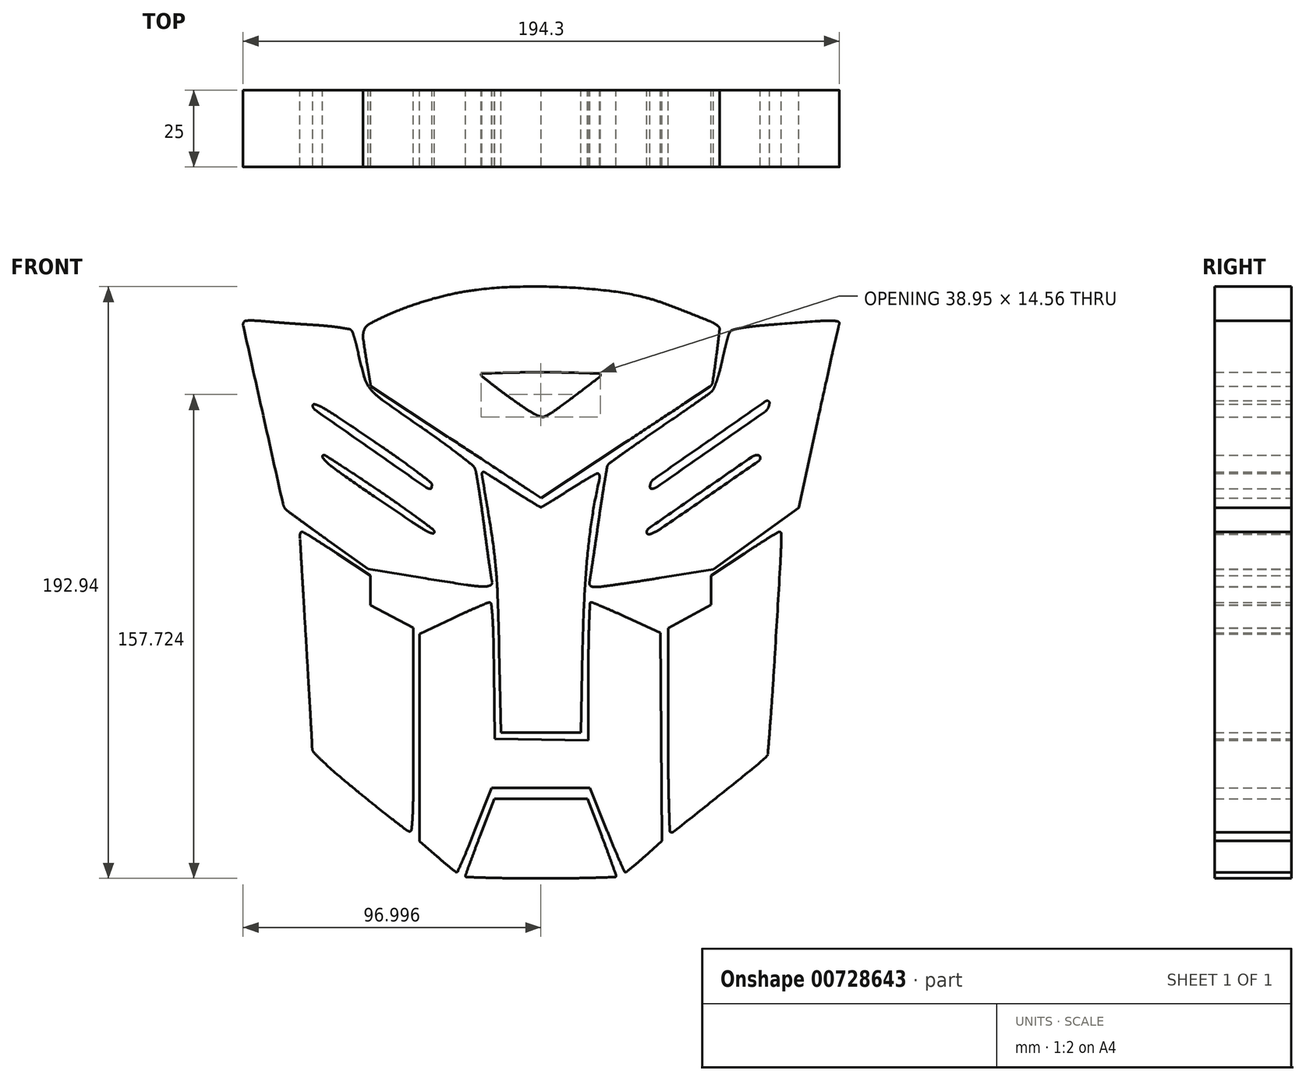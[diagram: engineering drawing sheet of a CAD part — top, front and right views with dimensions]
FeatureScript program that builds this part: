
annotation { "Feature Type Name" : "Feature", "Feature Type Description" : "" }
export const myFeature = defineFeature(function(context is Context, id is Id, definition is map)
    precondition{}
    {
        {
            var Q0;
            Q0=qCreatedBy(makeId("Front.planeOp"),FACE);
            var sketch = newSketch(context, id + "F0", { "sketchPlane" : qUnion([Q0])});
            skArc(sketch, "E0", {"start": v(-21.15, 95.4) * mm, "mid": v(-24.78, 94.86) * mm, "end": v(-28.38, 94.18) * mm});
            skArc(sketch, "E1", {"start": v(-28.38, 94.18) * mm, "mid": v(-32.1, 93.34) * mm, "end": v(-35.76, 92.36) * mm});
            skArc(sketch, "E2", {"start": v(-35.76, 92.36) * mm, "mid": v(-39.46, 91.24) * mm, "end": v(-43.12, 89.99) * mm});
            skArc(sketch, "E3", {"start": v(-43.12, 89.99) * mm, "mid": v(-46.72, 88.61) * mm, "end": v(-50.27, 87.11) * mm});
            skArc(sketch, "E4", {"start": v(-50.27, 87.11) * mm, "mid": v(-53.12, 85.79) * mm, "end": v(-55.91, 84.36) * mm});
            skArc(sketch, "E5", {"start": v(-55.91, 84.36) * mm, "mid": v(-56.96, 83.53) * mm, "end": v(-57.66, 82.4) * mm});
            skArc(sketch, "E6", {"start": v(-57.66, 82.4) * mm, "mid": v(-58.03, 80.98) * mm, "end": v(-58.02, 79.51) * mm});
            skArc(sketch, "E7", {"start": v(-58.02, 79.51) * mm, "mid": v(-57.4, 75.24) * mm, "end": v(-56.72, 70.97) * mm});
            skLineSegment(sketch, "E8", {"start": v(-56.72, 70.97) * mm, "end": v(-55.55, 64) * mm});
            skLineSegment(sketch, "E9", {"start": v(-55.55, 64) * mm, "end": v(-30.46, 47.52) * mm});
            skArc(sketch, "E10", {"start": v(-30.46, 47.52) * mm, "mid": v(-25.56, 44.3) * mm, "end": v(-20.66, 41.08) * mm});
            skArc(sketch, "E11", {"start": v(-20.66, 41.08) * mm, "mid": v(-16.31, 38.22) * mm, "end": v(-11.96, 35.37) * mm});
            skArc(sketch, "E12", {"start": v(-11.96, 35.37) * mm, "mid": v(-8.28, 32.95) * mm, "end": v(-4.6, 30.54) * mm});
            skArc(sketch, "E13", {"start": v(-4.6, 30.54) * mm, "mid": v(-3.66, 29.92) * mm, "end": v(-2.71, 29.31) * mm});
            skLineSegment(sketch, "E14", {"start": v(-2.71, 29.31) * mm, "end": v(-0.04, 27.59) * mm});
            skLineSegment(sketch, "E15", {"start": v(-0.04, 27.59) * mm, "end": v(27.4, 45.66) * mm});
            skArc(sketch, "E16", {"start": v(27.4, 45.66) * mm, "mid": v(32.68, 49.14) * mm, "end": v(37.95, 52.61) * mm});
            skArc(sketch, "E17", {"start": v(37.95, 52.61) * mm, "mid": v(42.41, 55.56) * mm, "end": v(46.87, 58.5) * mm});
            skArc(sketch, "E18", {"start": v(46.87, 58.5) * mm, "mid": v(50.88, 61.16) * mm, "end": v(54.9, 63.8) * mm});
            skArc(sketch, "E19", {"start": v(54.9, 63.8) * mm, "mid": v(55.02, 63.9) * mm, "end": v(55.14, 64) * mm});
            skArc(sketch, "E20", {"start": v(55.14, 64) * mm, "mid": v(55.63, 64.65) * mm, "end": v(55.87, 65.41) * mm});
            skArc(sketch, "E21", {"start": v(55.87, 65.41) * mm, "mid": v(56.47, 69.61) * mm, "end": v(57.04, 73.82) * mm});
            skArc(sketch, "E22", {"start": v(57.04, 73.82) * mm, "mid": v(57.6, 78.1) * mm, "end": v(58.13, 82.38) * mm});
            skArc(sketch, "E23", {"start": v(58.13, 82.38) * mm, "mid": v(58.06, 82.98) * mm, "end": v(57.72, 83.48) * mm});
            skArc(sketch, "E24", {"start": v(57.72, 83.48) * mm, "mid": v(56.62, 84.3) * mm, "end": v(55.4, 84.94) * mm});
            skArc(sketch, "E25", {"start": v(55.4, 84.94) * mm, "mid": v(51.39, 86.59) * mm, "end": v(47.37, 88.2) * mm});
            skArc(sketch, "E26", {"start": v(47.37, 88.2) * mm, "mid": v(43.36, 89.75) * mm, "end": v(39.33, 91.24) * mm});
            skArc(sketch, "E27", {"start": v(39.33, 91.24) * mm, "mid": v(36.6, 92.14) * mm, "end": v(33.85, 92.91) * mm});
            skArc(sketch, "E28", {"start": v(33.85, 92.91) * mm, "mid": v(28.04, 94.18) * mm, "end": v(22.15, 95.06) * mm});
            skArc(sketch, "E29", {"start": v(22.15, 95.06) * mm, "mid": v(14.8, 95.78) * mm, "end": v(7.43, 96.25) * mm});
            skArc(sketch, "E30", {"start": v(7.43, 96.25) * mm, "mid": v(-0.18, 96.46) * mm, "end": v(-7.79, 96.4) * mm});
            skArc(sketch, "E31", {"start": v(-7.79, 96.4) * mm, "mid": v(-14.48, 96.07) * mm, "end": v(-21.15, 95.4) * mm});
            skArc(sketch, "E32", {"start": v(19.32, 67.78) * mm, "mid": v(19.18, 67.27) * mm, "end": v(18.84, 66.86) * mm});
            skArc(sketch, "E33", {"start": v(18.84, 66.86) * mm, "mid": v(15.12, 64.02) * mm, "end": v(11.38, 61.2) * mm});
            skArc(sketch, "E34", {"start": v(11.38, 61.2) * mm, "mid": v(7.93, 58.61) * mm, "end": v(4.44, 56.06) * mm});
            skArc(sketch, "E35", {"start": v(4.44, 56.06) * mm, "mid": v(2.9, 55.04) * mm, "end": v(1.28, 54.16) * mm});
            skArc(sketch, "E36", {"start": v(1.28, 54.16) * mm, "mid": v(0.62, 53.98) * mm, "end": v(-0.06, 54.05) * mm});
            skArc(sketch, "E37", {"start": v(-0.06, 54.05) * mm, "mid": v(-1.12, 54.43) * mm, "end": v(-2.14, 54.91) * mm});
            skArc(sketch, "E38", {"start": v(-2.14, 54.91) * mm, "mid": v(-3.69, 55.79) * mm, "end": v(-5.18, 56.75) * mm});
            skArc(sketch, "E39", {"start": v(-5.18, 56.75) * mm, "mid": v(-7.63, 58.44) * mm, "end": v(-10.06, 60.16) * mm});
            skArc(sketch, "E40", {"start": v(-10.06, 60.16) * mm, "mid": v(-11.9, 61.5) * mm, "end": v(-13.72, 62.85) * mm});
            skArc(sketch, "E41", {"start": v(-13.72, 62.85) * mm, "mid": v(-15.27, 64.03) * mm, "end": v(-16.8, 65.23) * mm});
            skArc(sketch, "E42", {"start": v(-16.8, 65.23) * mm, "mid": v(-18.1, 66.28) * mm, "end": v(-19.4, 67.32) * mm});
            skArc(sketch, "E43", {"start": v(-19.4, 67.32) * mm, "mid": v(-19.56, 67.53) * mm, "end": v(-19.63, 67.78) * mm});
            skArc(sketch, "E44", {"start": v(-19.63, 67.78) * mm, "mid": v(-19.55, 68) * mm, "end": v(-19.34, 68.09) * mm});
            skArc(sketch, "E45", {"start": v(-19.34, 68.09) * mm, "mid": v(-16.63, 68.2) * mm, "end": v(-13.91, 68.31) * mm});
            skArc(sketch, "E46", {"start": v(-13.91, 68.31) * mm, "mid": v(-10.77, 68.41) * mm, "end": v(-7.62, 68.48) * mm});
            skArc(sketch, "E47", {"start": v(-7.62, 68.48) * mm, "mid": v(-3.89, 68.52) * mm, "end": v(-0.15, 68.53) * mm});
            skArc(sketch, "E48", {"start": v(-0.15, 68.53) * mm, "mid": v(3.59, 68.52) * mm, "end": v(7.33, 68.48) * mm});
            skArc(sketch, "E49", {"start": v(7.33, 68.48) * mm, "mid": v(10.47, 68.41) * mm, "end": v(13.61, 68.31) * mm});
            skArc(sketch, "E50", {"start": v(13.61, 68.31) * mm, "mid": v(16.33, 68.2) * mm, "end": v(19.04, 68.09) * mm});
            skArc(sketch, "E51", {"start": v(19.04, 68.09) * mm, "mid": v(19.24, 68) * mm, "end": v(19.32, 67.78) * mm});
            skArc(sketch, "E52", {"start": v(-96.73, 85.14) * mm, "mid": v(-97.1, 84.5) * mm, "end": v(-97.11, 83.79) * mm});
            skArc(sketch, "E53", {"start": v(-97.11, 83.79) * mm, "mid": v(-93.86, 69.13) * mm, "end": v(-90.6, 54.47) * mm});
            skArc(sketch, "E54", {"start": v(-90.6, 54.47) * mm, "mid": v(-87.37, 39.96) * mm, "end": v(-84.12, 25.45) * mm});
            skArc(sketch, "E55", {"start": v(-84.12, 25.45) * mm, "mid": v(-83.72, 24.45) * mm, "end": v(-83.03, 23.63) * mm});
            skArc(sketch, "E56", {"start": v(-83.03, 23.63) * mm, "mid": v(-82.7, 23.34) * mm, "end": v(-82.35, 23.08) * mm});
            skArc(sketch, "E57", {"start": v(-82.35, 23.08) * mm, "mid": v(-80.5, 21.72) * mm, "end": v(-78.64, 20.36) * mm});
            skArc(sketch, "E58", {"start": v(-78.64, 20.36) * mm, "mid": v(-76.47, 18.78) * mm, "end": v(-74.3, 17.2) * mm});
            skArc(sketch, "E59", {"start": v(-74.3, 17.2) * mm, "mid": v(-71.8, 15.4) * mm, "end": v(-69.31, 13.6) * mm});
            skLineSegment(sketch, "E60", {"start": v(-69.31, 13.6) * mm, "end": v(-56.47, 4.38) * mm});
            skLineSegment(sketch, "E61", {"start": v(-56.47, 4.38) * mm, "end": v(-38.5, 1.45) * mm});
            skArc(sketch, "E62", {"start": v(-38.5, 1.45) * mm, "mid": v(-31.44, 0.32) * mm, "end": v(-24.38, -0.78) * mm});
            skArc(sketch, "E63", {"start": v(-24.38, -0.78) * mm, "mid": v(-21.68, -1.13) * mm, "end": v(-18.96, -1.34) * mm});
            skArc(sketch, "E64", {"start": v(-18.96, -1.34) * mm, "mid": v(-17.77, -1.27) * mm, "end": v(-16.63, -0.96) * mm});
            skArc(sketch, "E65", {"start": v(-16.63, -0.96) * mm, "mid": v(-16.08, -0.45) * mm, "end": v(-16.01, 0.28) * mm});
            skArc(sketch, "E66", {"start": v(-16.01, 0.28) * mm, "mid": v(-16.17, 0.9) * mm, "end": v(-16.28, 1.54) * mm});
            skArc(sketch, "E67", {"start": v(-16.28, 1.54) * mm, "mid": v(-16.64, 3.95) * mm, "end": v(-17, 6.37) * mm});
            skArc(sketch, "E68", {"start": v(-17, 6.37) * mm, "mid": v(-17.4, 9.22) * mm, "end": v(-17.79, 12.08) * mm});
            skArc(sketch, "E69", {"start": v(-17.79, 12.08) * mm, "mid": v(-18.22, 15.3) * mm, "end": v(-18.64, 18.53) * mm});
            skArc(sketch, "E70", {"start": v(-18.64, 18.53) * mm, "mid": v(-19.07, 21.77) * mm, "end": v(-19.51, 25) * mm});
            skArc(sketch, "E71", {"start": v(-19.51, 25) * mm, "mid": v(-19.94, 27.9) * mm, "end": v(-20.39, 30.8) * mm});
            skArc(sketch, "E72", {"start": v(-20.39, 30.8) * mm, "mid": v(-20.78, 33.22) * mm, "end": v(-21.19, 35.64) * mm});
            skArc(sketch, "E73", {"start": v(-21.19, 35.64) * mm, "mid": v(-21.35, 36.38) * mm, "end": v(-21.6, 37.1) * mm});
            skArc(sketch, "E74", {"start": v(-21.6, 37.1) * mm, "mid": v(-21.97, 37.76) * mm, "end": v(-22.5, 38.3) * mm});
            skArc(sketch, "E75", {"start": v(-22.5, 38.3) * mm, "mid": v(-24.84, 40.16) * mm, "end": v(-27.2, 42) * mm});
            skArc(sketch, "E76", {"start": v(-27.2, 42) * mm, "mid": v(-30.03, 44.13) * mm, "end": v(-32.9, 46.23) * mm});
            skArc(sketch, "E77", {"start": v(-32.9, 46.23) * mm, "mid": v(-36.19, 48.57) * mm, "end": v(-39.5, 50.87) * mm});
            skArc(sketch, "E78", {"start": v(-39.5, 50.87) * mm, "mid": v(-45.65, 55.14) * mm, "end": v(-51.77, 59.45) * mm});
            skArc(sketch, "E79", {"start": v(-51.77, 59.45) * mm, "mid": v(-53.78, 61.1) * mm, "end": v(-55.57, 63) * mm});
            skArc(sketch, "E80", {"start": v(-55.57, 63) * mm, "mid": v(-56.82, 64.87) * mm, "end": v(-57.66, 66.96) * mm});
            skArc(sketch, "E81", {"start": v(-57.66, 66.96) * mm, "mid": v(-58.79, 71.2) * mm, "end": v(-59.78, 75.45) * mm});
            skArc(sketch, "E82", {"start": v(-59.78, 75.45) * mm, "mid": v(-60.03, 76.56) * mm, "end": v(-60.3, 77.67) * mm});
            skArc(sketch, "E83", {"start": v(-60.3, 77.67) * mm, "mid": v(-60.57, 78.7) * mm, "end": v(-60.87, 79.72) * mm});
            skArc(sketch, "E84", {"start": v(-60.87, 79.72) * mm, "mid": v(-61.14, 80.57) * mm, "end": v(-61.42, 81.4) * mm});
            skArc(sketch, "E85", {"start": v(-61.42, 81.4) * mm, "mid": v(-61.59, 81.79) * mm, "end": v(-61.81, 82.14) * mm});
            skArc(sketch, "E86", {"start": v(-61.81, 82.14) * mm, "mid": v(-62.14, 82.44) * mm, "end": v(-62.56, 82.6) * mm});
            skArc(sketch, "E87", {"start": v(-62.56, 82.6) * mm, "mid": v(-64.06, 82.87) * mm, "end": v(-65.56, 83.11) * mm});
            skArc(sketch, "E88", {"start": v(-65.56, 83.11) * mm, "mid": v(-67.39, 83.37) * mm, "end": v(-69.22, 83.57) * mm});
            skArc(sketch, "E89", {"start": v(-69.22, 83.57) * mm, "mid": v(-71.3, 83.76) * mm, "end": v(-73.4, 83.9) * mm});
            skArc(sketch, "E90", {"start": v(-73.4, 83.9) * mm, "mid": v(-75.68, 84.05) * mm, "end": v(-77.95, 84.2) * mm});
            skArc(sketch, "E91", {"start": v(-77.95, 84.2) * mm, "mid": v(-80.35, 84.38) * mm, "end": v(-82.75, 84.55) * mm});
            skArc(sketch, "E92", {"start": v(-82.75, 84.55) * mm, "mid": v(-84.93, 84.72) * mm, "end": v(-87.11, 84.9) * mm});
            skArc(sketch, "E93", {"start": v(-87.11, 84.9) * mm, "mid": v(-88.63, 85.02) * mm, "end": v(-90.15, 85.16) * mm});
            skArc(sketch, "E94", {"start": v(-90.15, 85.16) * mm, "mid": v(-91.32, 85.26) * mm, "end": v(-92.49, 85.34) * mm});
            skArc(sketch, "E95", {"start": v(-92.49, 85.34) * mm, "mid": v(-93.52, 85.38) * mm, "end": v(-94.56, 85.4) * mm});
            skArc(sketch, "E96", {"start": v(-94.56, 85.4) * mm, "mid": v(-95.4, 85.38) * mm, "end": v(-96.25, 85.35) * mm});
            skArc(sketch, "E97", {"start": v(-96.25, 85.35) * mm, "mid": v(-96.51, 85.29) * mm, "end": v(-96.73, 85.14) * mm});
            skArc(sketch, "E98", {"start": v(-53.56, 45.36) * mm, "mid": v(-50.12, 43) * mm, "end": v(-46.7, 40.6) * mm});
            skArc(sketch, "E99", {"start": v(-46.7, 40.6) * mm, "mid": v(-43.79, 38.51) * mm, "end": v(-40.9, 36.38) * mm});
            skArc(sketch, "E100", {"start": v(-40.9, 36.38) * mm, "mid": v(-38.47, 34.53) * mm, "end": v(-36.04, 32.67) * mm});
            skArc(sketch, "E101", {"start": v(-36.04, 32.67) * mm, "mid": v(-35.75, 32.32) * mm, "end": v(-35.65, 31.87) * mm});
            skArc(sketch, "E102", {"start": v(-35.65, 31.87) * mm, "mid": v(-35.65, 31.61) * mm, "end": v(-35.67, 31.36) * mm});
            skArc(sketch, "E103", {"start": v(-35.67, 31.36) * mm, "mid": v(-35.7, 31.14) * mm, "end": v(-35.75, 30.92) * mm});
            skArc(sketch, "E104", {"start": v(-35.75, 30.92) * mm, "mid": v(-35.8, 30.77) * mm, "end": v(-35.86, 30.62) * mm});
            skArc(sketch, "E105", {"start": v(-35.86, 30.62) * mm, "mid": v(-35.92, 30.56) * mm, "end": v(-36, 30.53) * mm});
            skArc(sketch, "E106", {"start": v(-36, 30.53) * mm, "mid": v(-36.86, 30.67) * mm, "end": v(-37.65, 31.05) * mm});
            skArc(sketch, "E107", {"start": v(-37.65, 31.05) * mm, "mid": v(-46.62, 37.3) * mm, "end": v(-55.58, 43.56) * mm});
            skArc(sketch, "E108", {"start": v(-55.58, 43.56) * mm, "mid": v(-64.56, 49.85) * mm, "end": v(-73.53, 56.14) * mm});
            skArc(sketch, "E109", {"start": v(-73.53, 56.14) * mm, "mid": v(-74.11, 56.71) * mm, "end": v(-74.48, 57.44) * mm});
            skArc(sketch, "E110", {"start": v(-74.48, 57.44) * mm, "mid": v(-74.36, 57.96) * mm, "end": v(-73.84, 58.1) * mm});
            skArc(sketch, "E111", {"start": v(-73.84, 58.1) * mm, "mid": v(-72.58, 57.69) * mm, "end": v(-71.39, 57.1) * mm});
            skArc(sketch, "E112", {"start": v(-71.39, 57.1) * mm, "mid": v(-68.65, 55.46) * mm, "end": v(-65.97, 53.73) * mm});
            skArc(sketch, "E113", {"start": v(-65.97, 53.73) * mm, "mid": v(-59.76, 49.56) * mm, "end": v(-53.56, 45.36) * mm});
            skArc(sketch, "E114", {"start": v(-52.65, 29.76) * mm, "mid": v(-49.3, 27.47) * mm, "end": v(-45.96, 25.15) * mm});
            skArc(sketch, "E115", {"start": v(-45.96, 25.15) * mm, "mid": v(-43.1, 23.11) * mm, "end": v(-40.26, 21.04) * mm});
            skArc(sketch, "E116", {"start": v(-40.26, 21.04) * mm, "mid": v(-37.85, 19.25) * mm, "end": v(-35.44, 17.44) * mm});
            skArc(sketch, "E117", {"start": v(-35.44, 17.44) * mm, "mid": v(-35.08, 17.07) * mm, "end": v(-34.84, 16.6) * mm});
            skArc(sketch, "E118", {"start": v(-34.84, 16.6) * mm, "mid": v(-34.93, 16.14) * mm, "end": v(-35.38, 16) * mm});
            skArc(sketch, "E119", {"start": v(-35.38, 16) * mm, "mid": v(-36.43, 16.31) * mm, "end": v(-37.42, 16.8) * mm});
            skArc(sketch, "E120", {"start": v(-37.42, 16.8) * mm, "mid": v(-39.85, 18.27) * mm, "end": v(-42.23, 19.81) * mm});
            skArc(sketch, "E121", {"start": v(-42.23, 19.81) * mm, "mid": v(-48.32, 23.92) * mm, "end": v(-54.4, 28.05) * mm});
            skArc(sketch, "E122", {"start": v(-54.4, 28.05) * mm, "mid": v(-59.42, 31.49) * mm, "end": v(-64.42, 34.96) * mm});
            skArc(sketch, "E123", {"start": v(-64.42, 34.96) * mm, "mid": v(-66.94, 36.8) * mm, "end": v(-69.4, 38.74) * mm});
            skArc(sketch, "E124", {"start": v(-69.4, 38.74) * mm, "mid": v(-70.39, 39.67) * mm, "end": v(-71.24, 40.72) * mm});
            skArc(sketch, "E125", {"start": v(-71.24, 40.72) * mm, "mid": v(-71.28, 41.26) * mm, "end": v(-70.82, 41.53) * mm});
            skArc(sketch, "E126", {"start": v(-70.82, 41.53) * mm, "mid": v(-70.51, 41.49) * mm, "end": v(-70.23, 41.36) * mm});
            skArc(sketch, "E127", {"start": v(-70.23, 41.36) * mm, "mid": v(-67.68, 39.72) * mm, "end": v(-65.14, 38.07) * mm});
            skArc(sketch, "E128", {"start": v(-65.14, 38.07) * mm, "mid": v(-62.24, 36.18) * mm, "end": v(-59.36, 34.27) * mm});
            skArc(sketch, "E129", {"start": v(-59.36, 34.27) * mm, "mid": v(-56, 32.02) * mm, "end": v(-52.65, 29.76) * mm});
            skArc(sketch, "E130", {"start": v(76.03, 84.13) * mm, "mid": v(72.61, 83.85) * mm, "end": v(69.2, 83.52) * mm});
            skArc(sketch, "E131", {"start": v(69.2, 83.52) * mm, "mid": v(67.1, 83.28) * mm, "end": v(65.02, 82.95) * mm});
            skArc(sketch, "E132", {"start": v(65.02, 82.95) * mm, "mid": v(63.7, 82.67) * mm, "end": v(62.37, 82.33) * mm});
            skArc(sketch, "E133", {"start": v(62.37, 82.33) * mm, "mid": v(61.8, 82.03) * mm, "end": v(61.4, 81.53) * mm});
            skArc(sketch, "E134", {"start": v(61.4, 81.53) * mm, "mid": v(61.16, 81.05) * mm, "end": v(60.99, 80.54) * mm});
            skArc(sketch, "E135", {"start": v(60.99, 80.54) * mm, "mid": v(60.64, 79.3) * mm, "end": v(60.3, 78.06) * mm});
            skArc(sketch, "E136", {"start": v(60.3, 78.06) * mm, "mid": v(59.92, 76.57) * mm, "end": v(59.56, 75.07) * mm});
            skArc(sketch, "E137", {"start": v(59.56, 75.07) * mm, "mid": v(59.19, 73.44) * mm, "end": v(58.83, 71.81) * mm});
            skArc(sketch, "E138", {"start": v(58.83, 71.81) * mm, "mid": v(58.46, 70.18) * mm, "end": v(58.04, 68.56) * mm});
            skArc(sketch, "E139", {"start": v(58.04, 68.56) * mm, "mid": v(57.6, 67.07) * mm, "end": v(57.12, 65.6) * mm});
            skArc(sketch, "E140", {"start": v(57.12, 65.6) * mm, "mid": v(56.67, 64.39) * mm, "end": v(56.19, 63.2) * mm});
            skArc(sketch, "E141", {"start": v(56.19, 63.2) * mm, "mid": v(55.88, 62.65) * mm, "end": v(55.46, 62.2) * mm});
            skArc(sketch, "E142", {"start": v(55.46, 62.2) * mm, "mid": v(54.89, 61.72) * mm, "end": v(54.28, 61.27) * mm});
            skArc(sketch, "E143", {"start": v(54.28, 61.27) * mm, "mid": v(51.99, 59.66) * mm, "end": v(49.7, 58.04) * mm});
            skArc(sketch, "E144", {"start": v(49.7, 58.04) * mm, "mid": v(46.97, 56.14) * mm, "end": v(44.24, 54.25) * mm});
            skArc(sketch, "E145", {"start": v(44.24, 54.25) * mm, "mid": v(41.16, 52.13) * mm, "end": v(38.07, 50.02) * mm});
            skArc(sketch, "E146", {"start": v(38.07, 50.02) * mm, "mid": v(35.02, 47.93) * mm, "end": v(31.98, 45.83) * mm});
            skArc(sketch, "E147", {"start": v(31.98, 45.83) * mm, "mid": v(29.37, 44) * mm, "end": v(26.76, 42.14) * mm});
            skArc(sketch, "E148", {"start": v(26.76, 42.14) * mm, "mid": v(24.52, 40.53) * mm, "end": v(22.27, 38.92) * mm});
            skArc(sketch, "E149", {"start": v(22.27, 38.92) * mm, "mid": v(21.97, 38.65) * mm, "end": v(21.73, 38.33) * mm});
            skArc(sketch, "E150", {"start": v(21.73, 38.33) * mm, "mid": v(21.55, 37.97) * mm, "end": v(21.44, 37.59) * mm});
            skArc(sketch, "E151", {"start": v(21.44, 37.59) * mm, "mid": v(21.03, 35.18) * mm, "end": v(20.63, 32.78) * mm});
            skArc(sketch, "E152", {"start": v(20.63, 32.78) * mm, "mid": v(20.17, 29.98) * mm, "end": v(19.73, 27.19) * mm});
            skArc(sketch, "E153", {"start": v(19.73, 27.19) * mm, "mid": v(19.25, 23.96) * mm, "end": v(18.78, 20.72) * mm});
            skArc(sketch, "E154", {"start": v(18.78, 20.72) * mm, "mid": v(18.31, 17.43) * mm, "end": v(17.83, 14.13) * mm});
            skArc(sketch, "E155", {"start": v(17.83, 14.13) * mm, "mid": v(17.4, 11.13) * mm, "end": v(16.96, 8.13) * mm});
            skArc(sketch, "E156", {"start": v(16.96, 8.13) * mm, "mid": v(16.58, 5.61) * mm, "end": v(16.2, 3.1) * mm});
            skArc(sketch, "E157", {"start": v(16.2, 3.1) * mm, "mid": v(16.06, 2.19) * mm, "end": v(15.9, 1.28) * mm});
            skArc(sketch, "E158", {"start": v(15.9, 1.28) * mm, "mid": v(15.78, 0.5) * mm, "end": v(15.7, -0.28) * mm});
            skArc(sketch, "E159", {"start": v(15.7, -0.28) * mm, "mid": v(15.75, -0.67) * mm, "end": v(15.94, -1) * mm});
            skArc(sketch, "E160", {"start": v(15.94, -1) * mm, "mid": v(16.23, -1.25) * mm, "end": v(16.6, -1.37) * mm});
            skArc(sketch, "E161", {"start": v(16.6, -1.37) * mm, "mid": v(17.36, -1.43) * mm, "end": v(18.13, -1.44) * mm});
            skArc(sketch, "E162", {"start": v(18.13, -1.44) * mm, "mid": v(19.04, -1.4) * mm, "end": v(19.94, -1.32) * mm});
            skArc(sketch, "E163", {"start": v(19.94, -1.32) * mm, "mid": v(22.58, -0.96) * mm, "end": v(25.22, -0.59) * mm});
            skArc(sketch, "E164", {"start": v(25.22, -0.59) * mm, "mid": v(28.37, -0.13) * mm, "end": v(31.5, 0.34) * mm});
            skArc(sketch, "E165", {"start": v(31.5, 0.34) * mm, "mid": v(34.98, 0.89) * mm, "end": v(38.45, 1.44) * mm});
            skLineSegment(sketch, "E166", {"start": v(38.45, 1.44) * mm, "end": v(56.04, 4.31) * mm});
            skLineSegment(sketch, "E167", {"start": v(56.04, 4.31) * mm, "end": v(69.95, 14.35) * mm});
            skLineSegment(sketch, "E168", {"start": v(69.95, 14.35) * mm, "end": v(83.85, 24.4) * mm});
            skLineSegment(sketch, "E169", {"start": v(83.85, 24.4) * mm, "end": v(90.25, 53.71) * mm});
            skArc(sketch, "E170", {"start": v(90.25, 53.71) * mm, "mid": v(91.5, 59.38) * mm, "end": v(92.74, 65.04) * mm});
            skArc(sketch, "E171", {"start": v(92.74, 65.04) * mm, "mid": v(93.82, 69.92) * mm, "end": v(94.9, 74.79) * mm});
            skArc(sketch, "E172", {"start": v(94.9, 74.79) * mm, "mid": v(95.86, 79.04) * mm, "end": v(96.82, 83.3) * mm});
            skArc(sketch, "E173", {"start": v(96.82, 83.3) * mm, "mid": v(96.95, 83.8) * mm, "end": v(97.1, 84.28) * mm});
            skArc(sketch, "E174", {"start": v(97.1, 84.28) * mm, "mid": v(97.07, 84.8) * mm, "end": v(96.65, 85.11) * mm});
            skArc(sketch, "E175", {"start": v(96.65, 85.11) * mm, "mid": v(95.47, 85.3) * mm, "end": v(94.28, 85.35) * mm});
            skArc(sketch, "E176", {"start": v(94.28, 85.35) * mm, "mid": v(91.75, 85.3) * mm, "end": v(89.22, 85.15) * mm});
            skArc(sketch, "E177", {"start": v(89.22, 85.15) * mm, "mid": v(82.62, 84.65) * mm, "end": v(76.03, 84.13) * mm});
            skArc(sketch, "E178", {"start": v(74.05, 57.2) * mm, "mid": v(73.57, 56.35) * mm, "end": v(72.87, 55.68) * mm});
            skArc(sketch, "E179", {"start": v(72.87, 55.68) * mm, "mid": v(64.07, 49.52) * mm, "end": v(55.26, 43.37) * mm});
            skArc(sketch, "E180", {"start": v(55.26, 43.37) * mm, "mid": v(46.44, 37.23) * mm, "end": v(37.61, 31.1) * mm});
            skArc(sketch, "E181", {"start": v(37.61, 31.1) * mm, "mid": v(36.76, 30.68) * mm, "end": v(35.82, 30.53) * mm});
            skArc(sketch, "E182", {"start": v(35.82, 30.53) * mm, "mid": v(35.7, 30.56) * mm, "end": v(35.6, 30.65) * mm});
            skArc(sketch, "E183", {"start": v(35.6, 30.65) * mm, "mid": v(35.53, 30.8) * mm, "end": v(35.48, 30.97) * mm});
            skArc(sketch, "E184", {"start": v(35.48, 30.97) * mm, "mid": v(35.45, 31.2) * mm, "end": v(35.45, 31.45) * mm});
            skArc(sketch, "E185", {"start": v(35.45, 31.45) * mm, "mid": v(35.48, 31.74) * mm, "end": v(35.53, 32.02) * mm});
            skArc(sketch, "E186", {"start": v(35.53, 32.02) * mm, "mid": v(35.92, 32.94) * mm, "end": v(36.62, 33.66) * mm});
            skArc(sketch, "E187", {"start": v(36.62, 33.66) * mm, "mid": v(45.66, 40) * mm, "end": v(54.72, 46.31) * mm});
            skArc(sketch, "E188", {"start": v(54.72, 46.31) * mm, "mid": v(63.9, 52.7) * mm, "end": v(73.08, 59.07) * mm});
            skArc(sketch, "E189", {"start": v(73.08, 59.07) * mm, "mid": v(73.67, 59.23) * mm, "end": v(74.23, 58.98) * mm});
            skArc(sketch, "E190", {"start": v(74.23, 58.98) * mm, "mid": v(74.3, 58.87) * mm, "end": v(74.33, 58.75) * mm});
            skArc(sketch, "E191", {"start": v(74.33, 58.75) * mm, "mid": v(74.34, 58.53) * mm, "end": v(74.33, 58.3) * mm});
            skArc(sketch, "E192", {"start": v(74.33, 58.3) * mm, "mid": v(74.3, 58.03) * mm, "end": v(74.23, 57.77) * mm});
            skArc(sketch, "E193", {"start": v(74.23, 57.77) * mm, "mid": v(74.15, 57.48) * mm, "end": v(74.05, 57.2) * mm});
            skArc(sketch, "E194", {"start": v(71.35, 40.59) * mm, "mid": v(71.22, 40.03) * mm, "end": v(70.84, 39.6) * mm});
            skArc(sketch, "E195", {"start": v(70.84, 39.6) * mm, "mid": v(62.7, 33.94) * mm, "end": v(54.55, 28.3) * mm});
            skArc(sketch, "E196", {"start": v(54.55, 28.3) * mm, "mid": v(46.88, 22.99) * mm, "end": v(39.18, 17.7) * mm});
            skArc(sketch, "E197", {"start": v(39.18, 17.7) * mm, "mid": v(37.45, 16.65) * mm, "end": v(35.6, 15.8) * mm});
            skArc(sketch, "E198", {"start": v(35.6, 15.8) * mm, "mid": v(35.37, 15.74) * mm, "end": v(35.12, 15.7) * mm});
            skArc(sketch, "E199", {"start": v(35.12, 15.7) * mm, "mid": v(34.92, 15.71) * mm, "end": v(34.72, 15.77) * mm});
            skArc(sketch, "E200", {"start": v(34.72, 15.77) * mm, "mid": v(34.57, 15.87) * mm, "end": v(34.45, 16.02) * mm});
            skArc(sketch, "E201", {"start": v(34.45, 16.02) * mm, "mid": v(34.38, 16.2) * mm, "end": v(34.35, 16.38) * mm});
            skArc(sketch, "E202", {"start": v(34.35, 16.38) * mm, "mid": v(34.52, 17.06) * mm, "end": v(34.98, 17.59) * mm});
            skArc(sketch, "E203", {"start": v(34.98, 17.59) * mm, "mid": v(43.42, 23.48) * mm, "end": v(51.87, 29.36) * mm});
            skArc(sketch, "E204", {"start": v(51.87, 29.36) * mm, "mid": v(60.2, 35.14) * mm, "end": v(68.55, 40.92) * mm});
            skArc(sketch, "E205", {"start": v(68.55, 40.92) * mm, "mid": v(69.5, 41.38) * mm, "end": v(70.53, 41.53) * mm});
            skArc(sketch, "E206", {"start": v(70.53, 41.53) * mm, "mid": v(70.7, 41.51) * mm, "end": v(70.84, 41.46) * mm});
            skArc(sketch, "E207", {"start": v(70.84, 41.46) * mm, "mid": v(70.99, 41.37) * mm, "end": v(71.11, 41.25) * mm});
            skArc(sketch, "E208", {"start": v(71.11, 41.25) * mm, "mid": v(71.22, 41.1) * mm, "end": v(71.3, 40.95) * mm});
            skArc(sketch, "E209", {"start": v(71.3, 40.95) * mm, "mid": v(71.34, 40.77) * mm, "end": v(71.35, 40.59) * mm});
            skArc(sketch, "E210", {"start": v(-19.13, 33.83) * mm, "mid": v(-17.67, 25.16) * mm, "end": v(-16.26, 16.48) * mm});
            skArc(sketch, "E211", {"start": v(-16.26, 16.48) * mm, "mid": v(-15.5, 11.18) * mm, "end": v(-14.91, 5.86) * mm});
            skArc(sketch, "E212", {"start": v(-14.91, 5.86) * mm, "mid": v(-14.48, 0.56) * mm, "end": v(-14.2, -4.75) * mm});
            skArc(sketch, "E213", {"start": v(-14.2, -4.75) * mm, "mid": v(-13.92, -13.36) * mm, "end": v(-13.71, -21.97) * mm});
            skLineSegment(sketch, "E214", {"start": v(-13.71, -21.97) * mm, "end": v(-13.15, -48.97) * mm});
            skLineSegment(sketch, "E215", {"start": v(-13.15, -48.97) * mm, "end": v(-0.15, -48.97) * mm});
            skLineSegment(sketch, "E216", {"start": v(-0.15, -48.97) * mm, "end": v(12.85, -48.97) * mm});
            skLineSegment(sketch, "E217", {"start": v(12.85, -48.97) * mm, "end": v(13.45, -21.97) * mm});
            skArc(sketch, "E218", {"start": v(13.45, -21.97) * mm, "mid": v(13.7, -13.31) * mm, "end": v(14.07, -4.66) * mm});
            skArc(sketch, "E219", {"start": v(14.07, -4.66) * mm, "mid": v(14.5, 2.47) * mm, "end": v(15.12, 9.59) * mm});
            skArc(sketch, "E220", {"start": v(15.12, 9.59) * mm, "mid": v(15.82, 15.76) * mm, "end": v(16.69, 21.92) * mm});
            skArc(sketch, "E221", {"start": v(16.69, 21.92) * mm, "mid": v(17.68, 27.62) * mm, "end": v(18.87, 33.28) * mm});
            skArc(sketch, "E222", {"start": v(18.87, 33.28) * mm, "mid": v(18.95, 33.71) * mm, "end": v(19, 34.15) * mm});
            skArc(sketch, "E223", {"start": v(19, 34.15) * mm, "mid": v(19, 34.51) * mm, "end": v(18.95, 34.87) * mm});
            skArc(sketch, "E224", {"start": v(18.95, 34.87) * mm, "mid": v(18.87, 35.13) * mm, "end": v(18.74, 35.36) * mm});
            skArc(sketch, "E225", {"start": v(18.74, 35.36) * mm, "mid": v(18.6, 35.49) * mm, "end": v(18.4, 35.53) * mm});
            skArc(sketch, "E226", {"start": v(18.4, 35.53) * mm, "mid": v(18.07, 35.49) * mm, "end": v(17.75, 35.36) * mm});
            skArc(sketch, "E227", {"start": v(17.75, 35.36) * mm, "mid": v(16.47, 34.64) * mm, "end": v(15.2, 33.92) * mm});
            skArc(sketch, "E228", {"start": v(15.2, 33.92) * mm, "mid": v(13.71, 33.04) * mm, "end": v(12.23, 32.14) * mm});
            skArc(sketch, "E229", {"start": v(12.23, 32.14) * mm, "mid": v(10.56, 31.1) * mm, "end": v(8.9, 30.03) * mm});
            skArc(sketch, "E230", {"start": v(8.9, 30.03) * mm, "mid": v(7.25, 28.98) * mm, "end": v(5.6, 27.92) * mm});
            skArc(sketch, "E231", {"start": v(5.6, 27.92) * mm, "mid": v(4.17, 27.03) * mm, "end": v(2.74, 26.15) * mm});
            skArc(sketch, "E232", {"start": v(2.74, 26.15) * mm, "mid": v(1.49, 25.39) * mm, "end": v(0.24, 24.63) * mm});
            skArc(sketch, "E233", {"start": v(0.24, 24.63) * mm, "mid": v(0.07, 24.56) * mm, "end": v(-0.1, 24.53) * mm});
            skArc(sketch, "E234", {"start": v(-0.1, 24.53) * mm, "mid": v(-0.28, 24.56) * mm, "end": v(-0.44, 24.63) * mm});
            skArc(sketch, "E235", {"start": v(-0.44, 24.63) * mm, "mid": v(-1.66, 25.36) * mm, "end": v(-2.87, 26.1) * mm});
            skArc(sketch, "E236", {"start": v(-2.87, 26.1) * mm, "mid": v(-4.27, 26.95) * mm, "end": v(-5.65, 27.81) * mm});
            skArc(sketch, "E237", {"start": v(-5.65, 27.81) * mm, "mid": v(-7.26, 28.83) * mm, "end": v(-8.86, 29.85) * mm});
            skArc(sketch, "E238", {"start": v(-8.86, 29.85) * mm, "mid": v(-10.5, 30.9) * mm, "end": v(-12.13, 31.94) * mm});
            skArc(sketch, "E239", {"start": v(-12.13, 31.94) * mm, "mid": v(-13.6, 32.88) * mm, "end": v(-15.08, 33.82) * mm});
            skArc(sketch, "E240", {"start": v(-15.08, 33.82) * mm, "mid": v(-16.32, 34.6) * mm, "end": v(-17.56, 35.4) * mm});
            skArc(sketch, "E241", {"start": v(-17.56, 35.4) * mm, "mid": v(-17.97, 35.65) * mm, "end": v(-18.38, 35.9) * mm});
            skArc(sketch, "E242", {"start": v(-18.38, 35.9) * mm, "mid": v(-18.64, 36) * mm, "end": v(-18.91, 36.05) * mm});
            skArc(sketch, "E243", {"start": v(-18.91, 36.05) * mm, "mid": v(-19.1, 35.99) * mm, "end": v(-19.23, 35.83) * mm});
            skArc(sketch, "E244", {"start": v(-19.23, 35.83) * mm, "mid": v(-19.3, 35.5) * mm, "end": v(-19.31, 35.15) * mm});
            skArc(sketch, "E245", {"start": v(-19.31, 35.15) * mm, "mid": v(-19.24, 34.5) * mm, "end": v(-19.13, 33.83) * mm});
            skArc(sketch, "E246", {"start": v(-78.64, 15.28) * mm, "mid": v(-78.62, 14.8) * mm, "end": v(-78.6, 14.3) * mm});
            skArc(sketch, "E247", {"start": v(-78.6, 14.3) * mm, "mid": v(-78.32, 9.5) * mm, "end": v(-78.04, 4.7) * mm});
            skArc(sketch, "E248", {"start": v(-78.04, 4.7) * mm, "mid": v(-77.72, -0.76) * mm, "end": v(-77.4, -6.23) * mm});
            skArc(sketch, "E249", {"start": v(-77.4, -6.23) * mm, "mid": v(-77.02, -12.6) * mm, "end": v(-76.64, -18.97) * mm});
            skArc(sketch, "E250", {"start": v(-76.64, -18.97) * mm, "mid": v(-76.26, -25.36) * mm, "end": v(-75.88, -31.76) * mm});
            skArc(sketch, "E251", {"start": v(-75.88, -31.76) * mm, "mid": v(-75.56, -37.31) * mm, "end": v(-75.24, -42.87) * mm});
            skArc(sketch, "E252", {"start": v(-75.24, -42.87) * mm, "mid": v(-74.97, -47.66) * mm, "end": v(-74.7, -52.46) * mm});
            skArc(sketch, "E253", {"start": v(-74.7, -52.46) * mm, "mid": v(-74.66, -53.22) * mm, "end": v(-74.65, -53.99) * mm});
            skArc(sketch, "E254", {"start": v(-74.65, -53.99) * mm, "mid": v(-74.5, -54.75) * mm, "end": v(-74.09, -55.4) * mm});
            skArc(sketch, "E255", {"start": v(-74.09, -55.4) * mm, "mid": v(-72.57, -56.96) * mm, "end": v(-71.02, -58.49) * mm});
            skArc(sketch, "E256", {"start": v(-71.02, -58.49) * mm, "mid": v(-68.76, -60.57) * mm, "end": v(-66.45, -62.6) * mm});
            skArc(sketch, "E257", {"start": v(-66.45, -62.6) * mm, "mid": v(-63.06, -65.45) * mm, "end": v(-59.65, -68.27) * mm});
            skArc(sketch, "E258", {"start": v(-59.65, -68.27) * mm, "mid": v(-56.73, -70.64) * mm, "end": v(-53.8, -73) * mm});
            skArc(sketch, "E259", {"start": v(-53.8, -73) * mm, "mid": v(-51.21, -75.06) * mm, "end": v(-48.62, -77.1) * mm});
            skArc(sketch, "E260", {"start": v(-48.62, -77.1) * mm, "mid": v(-46.4, -78.82) * mm, "end": v(-44.17, -80.54) * mm});
            skArc(sketch, "E261", {"start": v(-44.17, -80.54) * mm, "mid": v(-43.68, -80.86) * mm, "end": v(-43.15, -81.1) * mm});
            skArc(sketch, "E262", {"start": v(-43.15, -81.1) * mm, "mid": v(-42.58, -81.05) * mm, "end": v(-42.27, -80.57) * mm});
            skArc(sketch, "E263", {"start": v(-42.27, -80.57) * mm, "mid": v(-42.05, -78.22) * mm, "end": v(-41.9, -75.85) * mm});
            skArc(sketch, "E264", {"start": v(-41.9, -75.85) * mm, "mid": v(-41.76, -71.62) * mm, "end": v(-41.7, -67.4) * mm});
            skArc(sketch, "E265", {"start": v(-41.7, -67.4) * mm, "mid": v(-41.66, -57.8) * mm, "end": v(-41.65, -48.2) * mm});
            skLineSegment(sketch, "E266", {"start": v(-41.65, -48.2) * mm, "end": v(-41.65, -14.71) * mm});
            skLineSegment(sketch, "E267", {"start": v(-41.65, -14.71) * mm, "end": v(-48.65, -11.04) * mm});
            skLineSegment(sketch, "E268", {"start": v(-48.65, -11.04) * mm, "end": v(-55.65, -7.36) * mm});
            skLineSegment(sketch, "E269", {"start": v(-55.65, -7.36) * mm, "end": v(-55.65, -2.55) * mm});
            skLineSegment(sketch, "E270", {"start": v(-55.65, -2.55) * mm, "end": v(-55.65, 2.26) * mm});
            skLineSegment(sketch, "E271", {"start": v(-55.65, 2.26) * mm, "end": v(-66.44, 9.4) * mm});
            skArc(sketch, "E272", {"start": v(-66.44, 9.4) * mm, "mid": v(-68.53, 10.77) * mm, "end": v(-70.63, 12.13) * mm});
            skArc(sketch, "E273", {"start": v(-70.63, 12.13) * mm, "mid": v(-72.45, 13.3) * mm, "end": v(-74.27, 14.44) * mm});
            skArc(sketch, "E274", {"start": v(-74.27, 14.44) * mm, "mid": v(-75.86, 15.42) * mm, "end": v(-77.44, 16.4) * mm});
            skArc(sketch, "E275", {"start": v(-77.44, 16.4) * mm, "mid": v(-77.68, 16.5) * mm, "end": v(-77.94, 16.53) * mm});
            skArc(sketch, "E276", {"start": v(-77.94, 16.53) * mm, "mid": v(-78.08, 16.5) * mm, "end": v(-78.2, 16.44) * mm});
            skArc(sketch, "E277", {"start": v(-78.2, 16.44) * mm, "mid": v(-78.34, 16.31) * mm, "end": v(-78.44, 16.17) * mm});
            skArc(sketch, "E278", {"start": v(-78.44, 16.17) * mm, "mid": v(-78.53, 15.97) * mm, "end": v(-78.59, 15.76) * mm});
            skArc(sketch, "E279", {"start": v(-78.59, 15.76) * mm, "mid": v(-78.62, 15.52) * mm, "end": v(-78.64, 15.28) * mm});
            skLineSegment(sketch, "E280", {"start": v(66.1, 9.38) * mm, "end": v(55.35, 2.24) * mm});
            skLineSegment(sketch, "E281", {"start": v(55.35, 2.24) * mm, "end": v(55.35, -2.54) * mm});
            skLineSegment(sketch, "E282", {"start": v(55.35, -2.54) * mm, "end": v(55.35, -7.33) * mm});
            skLineSegment(sketch, "E283", {"start": v(55.35, -7.33) * mm, "end": v(48.35, -11.1) * mm});
            skLineSegment(sketch, "E284", {"start": v(48.35, -11.1) * mm, "end": v(41.35, -14.89) * mm});
            skLineSegment(sketch, "E285", {"start": v(41.35, -14.89) * mm, "end": v(41.35, -48.18) * mm});
            skArc(sketch, "E286", {"start": v(41.35, -48.18) * mm, "mid": v(41.37, -55.32) * mm, "end": v(41.41, -62.46) * mm});
            skArc(sketch, "E287", {"start": v(41.41, -62.46) * mm, "mid": v(41.48, -67.64) * mm, "end": v(41.6, -72.82) * mm});
            skArc(sketch, "E288", {"start": v(41.6, -72.82) * mm, "mid": v(41.74, -76.92) * mm, "end": v(41.88, -81.02) * mm});
            skArc(sketch, "E289", {"start": v(41.88, -81.02) * mm, "mid": v(42.02, -81.34) * mm, "end": v(42.34, -81.47) * mm});
            skArc(sketch, "E290", {"start": v(42.34, -81.47) * mm, "mid": v(42.85, -81.38) * mm, "end": v(43.3, -81.13) * mm});
            skArc(sketch, "E291", {"start": v(43.3, -81.13) * mm, "mid": v(50, -75.81) * mm, "end": v(56.67, -70.49) * mm});
            skArc(sketch, "E292", {"start": v(56.67, -70.49) * mm, "mid": v(62.68, -65.68) * mm, "end": v(68.66, -60.85) * mm});
            skArc(sketch, "E293", {"start": v(68.66, -60.85) * mm, "mid": v(71.14, -58.78) * mm, "end": v(73.53, -56.6) * mm});
            skArc(sketch, "E294", {"start": v(73.53, -56.6) * mm, "mid": v(73.74, -56.32) * mm, "end": v(73.83, -55.98) * mm});
            skArc(sketch, "E295", {"start": v(73.83, -55.98) * mm, "mid": v(74.23, -50.93) * mm, "end": v(74.62, -45.87) * mm});
            skArc(sketch, "E296", {"start": v(74.62, -45.87) * mm, "mid": v(75.04, -40.15) * mm, "end": v(75.44, -34.43) * mm});
            skArc(sketch, "E297", {"start": v(75.44, -34.43) * mm, "mid": v(75.87, -27.7) * mm, "end": v(76.29, -20.97) * mm});
            skArc(sketch, "E298", {"start": v(76.29, -20.97) * mm, "mid": v(77.1, -7.28) * mm, "end": v(77.9, 6.41) * mm});
            skArc(sketch, "E299", {"start": v(77.9, 6.41) * mm, "mid": v(78.07, 9.63) * mm, "end": v(78.2, 12.84) * mm});
            skArc(sketch, "E300", {"start": v(78.2, 12.84) * mm, "mid": v(78.23, 14.4) * mm, "end": v(78.2, 15.96) * mm});
            skArc(sketch, "E301", {"start": v(78.2, 15.96) * mm, "mid": v(78.02, 16.36) * mm, "end": v(77.6, 16.53) * mm});
            skArc(sketch, "E302", {"start": v(77.6, 16.53) * mm, "mid": v(77.33, 16.49) * mm, "end": v(77.08, 16.38) * mm});
            skArc(sketch, "E303", {"start": v(77.08, 16.38) * mm, "mid": v(75.5, 15.4) * mm, "end": v(73.91, 14.43) * mm});
            skArc(sketch, "E304", {"start": v(73.91, 14.43) * mm, "mid": v(72.1, 13.28) * mm, "end": v(70.28, 12.12) * mm});
            skArc(sketch, "E305", {"start": v(70.28, 12.12) * mm, "mid": v(68.19, 10.76) * mm, "end": v(66.1, 9.38) * mm});
            skLineSegment(sketch, "E306", {"start": v(-28.9, -11.68) * mm, "end": v(-39.65, -16.76) * mm});
            skLineSegment(sketch, "E307", {"start": v(-39.65, -16.76) * mm, "end": v(-39.65, -50.53) * mm});
            skLineSegment(sketch, "E308", {"start": v(-39.65, -50.53) * mm, "end": v(-39.65, -84.3) * mm});
            skLineSegment(sketch, "E309", {"start": v(-39.65, -84.3) * mm, "end": v(-33.9, -89.37) * mm});
            skArc(sketch, "E310", {"start": v(-33.9, -89.37) * mm, "mid": v(-32.78, -90.35) * mm, "end": v(-31.65, -91.31) * mm});
            skArc(sketch, "E311", {"start": v(-31.65, -91.31) * mm, "mid": v(-30.66, -92.14) * mm, "end": v(-29.66, -92.95) * mm});
            skArc(sketch, "E312", {"start": v(-29.66, -92.95) * mm, "mid": v(-28.8, -93.64) * mm, "end": v(-27.95, -94.31) * mm});
            skArc(sketch, "E313", {"start": v(-27.95, -94.31) * mm, "mid": v(-27.77, -94.41) * mm, "end": v(-27.56, -94.45) * mm});
            skArc(sketch, "E314", {"start": v(-27.56, -94.45) * mm, "mid": v(-27.37, -94.4) * mm, "end": v(-27.24, -94.25) * mm});
            skArc(sketch, "E315", {"start": v(-27.24, -94.25) * mm, "mid": v(-26.4, -92.34) * mm, "end": v(-25.56, -90.42) * mm});
            skArc(sketch, "E316", {"start": v(-25.56, -90.42) * mm, "mid": v(-24.6, -88.21) * mm, "end": v(-23.68, -85.99) * mm});
            skArc(sketch, "E317", {"start": v(-23.68, -85.99) * mm, "mid": v(-22.61, -83.36) * mm, "end": v(-21.56, -80.72) * mm});
            skLineSegment(sketch, "E318", {"start": v(-21.56, -80.72) * mm, "end": v(-16.15, -66.97) * mm});
            skLineSegment(sketch, "E319", {"start": v(-16.15, -66.97) * mm, "end": v(-0.15, -66.97) * mm});
            skLineSegment(sketch, "E320", {"start": v(-0.15, -66.97) * mm, "end": v(15.85, -66.97) * mm});
            skLineSegment(sketch, "E321", {"start": v(15.85, -66.97) * mm, "end": v(21.35, -80.7) * mm});
            skArc(sketch, "E322", {"start": v(21.35, -80.7) * mm, "mid": v(22.42, -83.34) * mm, "end": v(23.5, -85.97) * mm});
            skArc(sketch, "E323", {"start": v(23.5, -85.97) * mm, "mid": v(24.44, -88.2) * mm, "end": v(25.4, -90.4) * mm});
            skArc(sketch, "E324", {"start": v(25.4, -90.4) * mm, "mid": v(26.25, -92.33) * mm, "end": v(27.1, -94.25) * mm});
            skArc(sketch, "E325", {"start": v(27.1, -94.25) * mm, "mid": v(27.22, -94.4) * mm, "end": v(27.4, -94.45) * mm});
            skArc(sketch, "E326", {"start": v(27.4, -94.45) * mm, "mid": v(27.6, -94.42) * mm, "end": v(27.77, -94.33) * mm});
            skArc(sketch, "E327", {"start": v(27.77, -94.33) * mm, "mid": v(28.62, -93.65) * mm, "end": v(29.47, -92.97) * mm});
            skArc(sketch, "E328", {"start": v(29.47, -92.97) * mm, "mid": v(30.46, -92.15) * mm, "end": v(31.44, -91.33) * mm});
            skArc(sketch, "E329", {"start": v(31.44, -91.33) * mm, "mid": v(32.56, -90.36) * mm, "end": v(33.67, -89.38) * mm});
            skLineSegment(sketch, "E330", {"start": v(33.67, -89.38) * mm, "end": v(39.38, -84.28) * mm});
            skLineSegment(sketch, "E331", {"start": v(39.38, -84.28) * mm, "end": v(39.12, -50.34) * mm});
            skLineSegment(sketch, "E332", {"start": v(39.12, -50.34) * mm, "end": v(38.85, -16.4) * mm});
            skLineSegment(sketch, "E333", {"start": v(38.85, -16.4) * mm, "end": v(27.98, -11.43) * mm});
            skArc(sketch, "E334", {"start": v(27.98, -11.43) * mm, "mid": v(25.87, -10.48) * mm, "end": v(23.75, -9.53) * mm});
            skArc(sketch, "E335", {"start": v(23.75, -9.53) * mm, "mid": v(21.9, -8.72) * mm, "end": v(20.04, -7.93) * mm});
            skArc(sketch, "E336", {"start": v(20.04, -7.93) * mm, "mid": v(18.45, -7.26) * mm, "end": v(16.85, -6.6) * mm});
            skArc(sketch, "E337", {"start": v(16.85, -6.6) * mm, "mid": v(16.55, -6.5) * mm, "end": v(16.23, -6.47) * mm});
            skArc(sketch, "E338", {"start": v(16.23, -6.47) * mm, "mid": v(15.98, -6.57) * mm, "end": v(15.87, -6.8) * mm});
            skArc(sketch, "E339", {"start": v(15.87, -6.8) * mm, "mid": v(15.74, -9.95) * mm, "end": v(15.6, -13.08) * mm});
            skArc(sketch, "E340", {"start": v(15.6, -13.08) * mm, "mid": v(15.5, -16.72) * mm, "end": v(15.42, -20.36) * mm});
            skArc(sketch, "E341", {"start": v(15.42, -20.36) * mm, "mid": v(15.37, -24.67) * mm, "end": v(15.35, -29) * mm});
            skLineSegment(sketch, "E342", {"start": v(15.35, -29) * mm, "end": v(15.35, -51.52) * mm});
            skLineSegment(sketch, "E343", {"start": v(15.35, -51.52) * mm, "end": v(0.1, -51.24) * mm});
            skLineSegment(sketch, "E344", {"start": v(0.1, -51.24) * mm, "end": v(-15.15, -50.97) * mm});
            skLineSegment(sketch, "E345", {"start": v(-15.15, -50.97) * mm, "end": v(-15.42, -28.72) * mm});
            skArc(sketch, "E346", {"start": v(-15.42, -28.72) * mm, "mid": v(-15.5, -23.22) * mm, "end": v(-15.6, -17.72) * mm});
            skArc(sketch, "E347", {"start": v(-15.6, -17.72) * mm, "mid": v(-15.71, -14.5) * mm, "end": v(-15.9, -11.29) * mm});
            skArc(sketch, "E348", {"start": v(-15.9, -11.29) * mm, "mid": v(-16.06, -9.19) * mm, "end": v(-16.26, -7.09) * mm});
            skArc(sketch, "E349", {"start": v(-16.26, -7.09) * mm, "mid": v(-16.48, -6.68) * mm, "end": v(-16.92, -6.53) * mm});
            skArc(sketch, "E350", {"start": v(-16.92, -6.53) * mm, "mid": v(-17.35, -6.6) * mm, "end": v(-17.76, -6.73) * mm});
            skArc(sketch, "E351", {"start": v(-17.76, -6.73) * mm, "mid": v(-19.35, -7.4) * mm, "end": v(-20.94, -8.07) * mm});
            skArc(sketch, "E352", {"start": v(-20.94, -8.07) * mm, "mid": v(-22.82, -8.9) * mm, "end": v(-24.69, -9.73) * mm});
            skArc(sketch, "E353", {"start": v(-24.69, -9.73) * mm, "mid": v(-26.8, -10.7) * mm, "end": v(-28.9, -11.68) * mm});
            skArc(sketch, "E354", {"start": v(-19.97, -82.72) * mm, "mid": v(-20.88, -85.09) * mm, "end": v(-21.78, -87.47) * mm});
            skArc(sketch, "E355", {"start": v(-21.78, -87.47) * mm, "mid": v(-22.54, -89.53) * mm, "end": v(-23.3, -91.59) * mm});
            skArc(sketch, "E356", {"start": v(-23.3, -91.59) * mm, "mid": v(-23.94, -93.38) * mm, "end": v(-24.57, -95.16) * mm});
            skArc(sketch, "E357", {"start": v(-24.57, -95.16) * mm, "mid": v(-24.64, -95.44) * mm, "end": v(-24.66, -95.72) * mm});
            skArc(sketch, "E358", {"start": v(-24.66, -95.72) * mm, "mid": v(-24.57, -95.93) * mm, "end": v(-24.36, -96.02) * mm});
            skArc(sketch, "E359", {"start": v(-24.36, -96.02) * mm, "mid": v(-20.9, -96.14) * mm, "end": v(-17.46, -96.25) * mm});
            skArc(sketch, "E360", {"start": v(-17.46, -96.25) * mm, "mid": v(-13.5, -96.35) * mm, "end": v(-9.54, -96.41) * mm});
            skArc(sketch, "E361", {"start": v(-9.54, -96.41) * mm, "mid": v(-4.85, -96.45) * mm, "end": v(-0.15, -96.47) * mm});
            skArc(sketch, "E362", {"start": v(-0.15, -96.47) * mm, "mid": v(4.55, -96.45) * mm, "end": v(9.25, -96.41) * mm});
            skArc(sketch, "E363", {"start": v(9.25, -96.41) * mm, "mid": v(13.2, -96.35) * mm, "end": v(17.16, -96.25) * mm});
            skArc(sketch, "E364", {"start": v(17.16, -96.25) * mm, "mid": v(20.61, -96.14) * mm, "end": v(24.07, -96.02) * mm});
            skArc(sketch, "E365", {"start": v(24.07, -96.02) * mm, "mid": v(24.28, -95.93) * mm, "end": v(24.37, -95.72) * mm});
            skArc(sketch, "E366", {"start": v(24.37, -95.72) * mm, "mid": v(24.35, -95.44) * mm, "end": v(24.28, -95.16) * mm});
            skArc(sketch, "E367", {"start": v(24.28, -95.16) * mm, "mid": v(23.65, -93.38) * mm, "end": v(23, -91.59) * mm});
            skArc(sketch, "E368", {"start": v(23, -91.59) * mm, "mid": v(22.26, -89.53) * mm, "end": v(21.5, -87.47) * mm});
            skArc(sketch, "E369", {"start": v(21.5, -87.47) * mm, "mid": v(20.62, -85.09) * mm, "end": v(19.72, -82.72) * mm});
            skLineSegment(sketch, "E370", {"start": v(19.72, -82.72) * mm, "end": v(15.06, -70.47) * mm});
            skLineSegment(sketch, "E371", {"start": v(15.06, -70.47) * mm, "end": v(-0.1, -70.47) * mm});
            skLineSegment(sketch, "E372", {"start": v(-0.1, -70.47) * mm, "end": v(-15.27, -70.47) * mm});
            skLineSegment(sketch, "E373", {"start": v(-15.27, -70.47) * mm, "end": v(-19.97, -82.72) * mm});
            skSolve(sketch);
        }
        {
            var Q0;
            Q0 = qSketchRegion(id + "F0", true);
            extrude(context, id + "F1", {"entities" : qUnion([Q0]), "depth" : 25 * mm, "offsetDistance" : 25 * mm});
        }
    });
